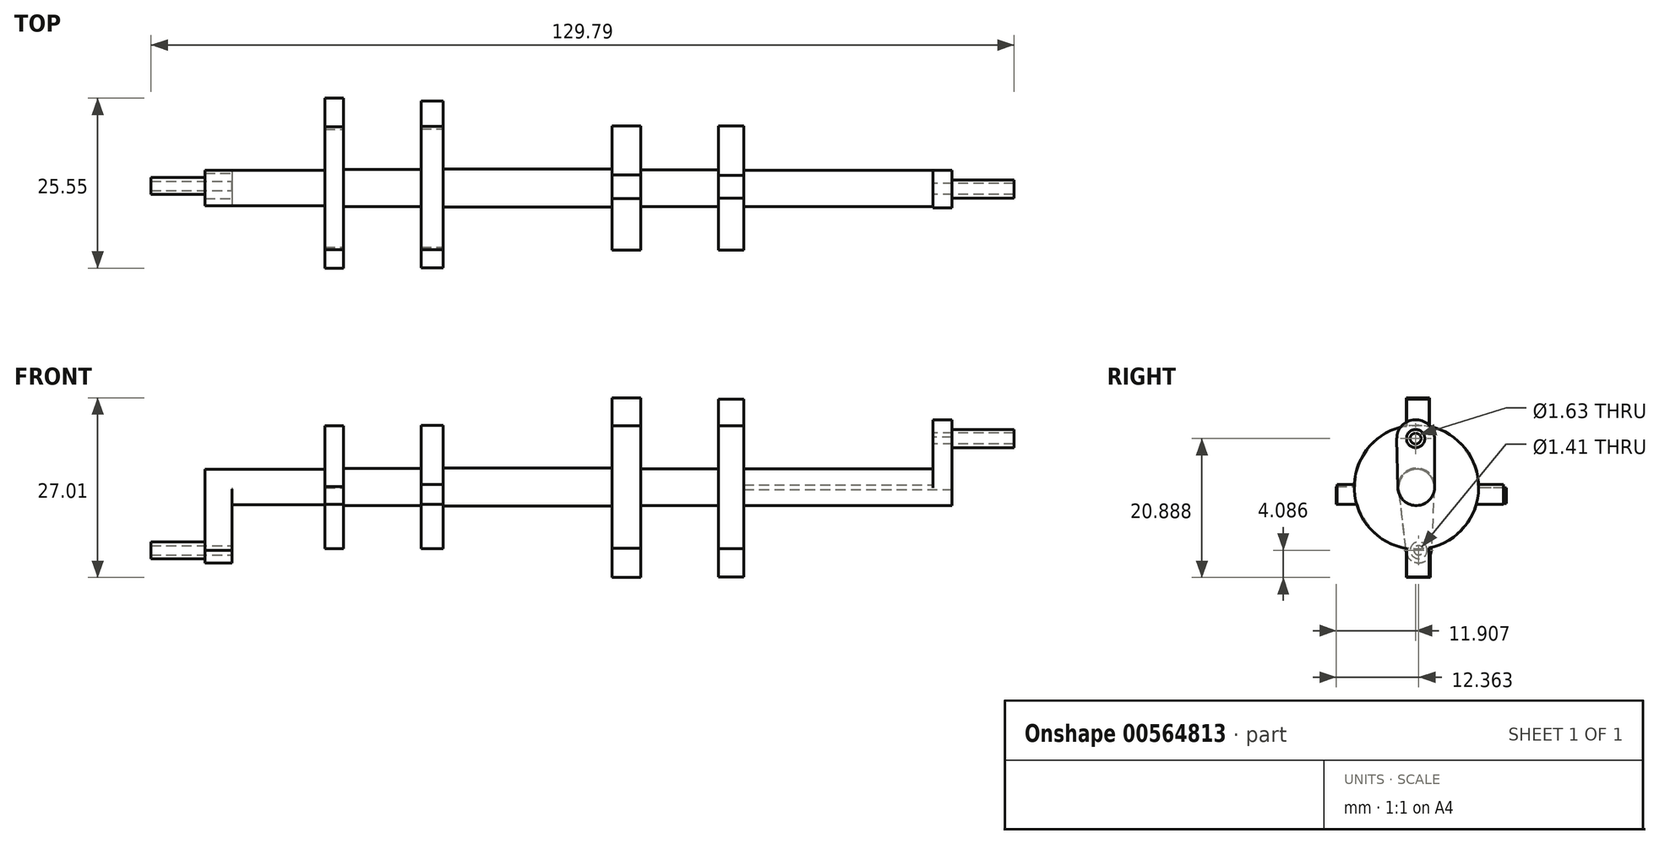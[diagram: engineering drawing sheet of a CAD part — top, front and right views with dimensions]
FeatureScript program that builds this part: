
annotation { "Feature Type Name" : "Feature", "Feature Type Description" : "" }
export const myFeature = defineFeature(function(context is Context, id is Id, definition is map)
    precondition{}
    {
        {
            var Q0;
            Q0=qCreatedBy(makeId("Right.planeOp"),FACE);
            var sketch = newSketch(context, id + "F0", { "sketchPlane" : qUnion([Q0])});
            skCircle(sketch, "E0", {"center": v(23.37, 56.05) * mm, "radius": 1.37 * mm});
            skCircle(sketch, "E1", {"center": v(23.46, 48.73) * mm, "radius": 2.75 * mm});
            skLineSegment(sketch, "E2", {"start": v(26.2, 48.37) * mm, "end": v(26.2, 56.23) * mm});
            skLineSegment(sketch, "E3", {"start": v(20.71, 48.66) * mm, "end": v(20.54, 55.98) * mm});
            skArc(sketch, "E4", {"start": v(26.2, 56.23) * mm, "mid": v(23.24, 58.88) * mm, "end": v(20.54, 55.98) * mm});
            skCircle(sketch, "E5", {"center": v(23.37, 56.05) * mm, "radius": 0.81 * mm});
            skSolve(sketch);
        }
        {
            var Q0;
            Q0=makeQuery(id+"F0.imprint","IMPRINT",FACE,{"disambiguationData":[TD([[makeQuery(id+"F0.imprint","IMPRINT",EDGE,{"derivedFrom":sQuery(id+"F0.wireOp",EDGE,"E0")}),1.0]])]});
            extrude(context, id + "F1", {"entities" : qUnion([Q0]), "depth" : 12.2 * mm, "offsetDistance" : 25.4 * mm});
        }
        {
            var Q0;
            Q0=makeQuery(id+"F0.imprint","IMPRINT",FACE,{"disambiguationData":[TD([[makeQuery(id+"F0.imprint","IMPRINT",EDGE,{"derivedFrom":sQuery(id+"F0.wireOp",EDGE,"E1")}),1.0]])]});
            extrude(context, id + "F2", {"entities" : qUnion([Q0]), "operationType" : NewBodyOperationType.ADD, "oppositeDirection" : true, "depth" : 28.45 * mm, "offsetDistance" : 25.4 * mm});
        }
        {
            var Q0;
            Q0=makeQuery(id+"F2.opExtrude","CAP_FACE",FACE,{"disambiguationData":[OSD([sQuery(id+"F0.wireOp",EDGE,"E1")])],"isStart":false});
            var sketch = newSketch(context, id + "F3", { "sketchPlane" : qUnion([Q0])});
            skSolve(sketch);
        }
        {
            var Q0;
            Q0=makeQuery(id+"F3.imprint","IMPRINT",FACE,{"disambiguationData":[TD([[makeQuery(id+"F3.imprint","IMPRINT",EDGE,{"derivedFrom":makeQuery(id+"F2.opExtrude","CAP_EDGE",EDGE,{"disambiguationData":[OSD([sQuery(id+"F0.wireOp",EDGE,"E1")])],"isStart":false})}),-1.0]])]});
            var sketch = newSketch(context, id + "F4", { "sketchPlane" : qUnion([Q0])});
            skCircle(sketch, "E6", {"center": v(-23.5, 48.74) * mm, "radius": 9.35 * mm});
            skLineSegment(sketch, "E7", {"start": v(-25.42, 57.9) * mm, "end": v(-25.42, 61.98) * mm});
            skLineSegment(sketch, "E8", {"start": v(-25.42, 61.98) * mm, "end": v(-22, 61.98) * mm});
            skLineSegment(sketch, "E9", {"start": v(-22, 61.98) * mm, "end": v(-22, 57.98) * mm});
            skLineSegment(sketch, "E10", {"start": v(-25.42, 39.59) * mm, "end": v(-25.42, 35.2) * mm});
            skLineSegment(sketch, "E11", {"start": v(-25.42, 35.2) * mm, "end": v(-22, 35.2) * mm});
            skLineSegment(sketch, "E12", {"start": v(-22, 35.2) * mm, "end": v(-22, 39.51) * mm});
            skSolve(sketch);
        }
        {
            var Q0;
            Q0=makeQuery(id+"F3.imprint","IMPRINT",FACE,{"disambiguationData":[TD([[makeQuery(id+"F3.imprint","IMPRINT",EDGE,{"derivedFrom":makeQuery(id+"F2.opExtrude","CAP_EDGE",EDGE,{"disambiguationData":[OSD([sQuery(id+"F0.wireOp",EDGE,"E1")])],"isStart":false})}),-1.0]])]});
            var Q1;
            {var subQ0=sQuery(id+"F4.wireOp",EDGE,"E10");Q1=makeQuery(id+"F4.imprint","IMPRINT",FACE,{"disambiguationData":[TD([[makeQuery(id+"F4.imprint","IMPRINT",EDGE,{"derivedFrom":subQ0}),1.0]])]});}
            var Q2;
            {var subQ0=sQuery(id+"F4.wireOp",EDGE,"E7");Q2=makeQuery(id+"F4.imprint","IMPRINT",FACE,{"disambiguationData":[TD([[makeQuery(id+"F4.imprint","IMPRINT",EDGE,{"derivedFrom":subQ0}),-1.0]])]});}
            var Q3;
            Q3=makeQuery(id+"F4.imprint","IMPRINT",FACE,{"disambiguationData":[TD([[makeQuery(id+"F4.imprint","IMPRINT",EDGE,{"derivedFrom":makeQuery(id+"F3.imprint","IMPRINT",EDGE,{"derivedFrom":makeQuery(id+"F2.opExtrude","CAP_EDGE",EDGE,{"disambiguationData":[OSD([sQuery(id+"F0.wireOp",EDGE,"E1")])],"isStart":false})})}),1.0]])]});
            extrude(context, id + "F5", {"entities" : qUnion([Q0, Q1, Q2, Q3]), "operationType" : NewBodyOperationType.ADD, "depth" : 3.8 * mm, "offsetDistance" : 25.4 * mm});
        }
        {
            var Q0;
            {var subQ0=sQuery(id+"F0.wireOp",EDGE,"E1");Q0=makeQuery(id+"F5.boolean.opBoolean","MERGE",FACE,{"derivedFrom":[makeQuery(id+"F5.opExtrude","CAP_FACE",FACE,{"disambiguationData":[OSD([subQ0])],"isStart":false}),makeQuery(id+"F5.opExtrude","CAP_FACE",FACE,{"disambiguationData":[OSD([subQ0,sQuery(id+"F4.wireOp",EDGE,"E6"),sQuery(id+"F4.wireOp",EDGE,"E7"),sQuery(id+"F4.wireOp",EDGE,"E8"),sQuery(id+"F4.wireOp",EDGE,"E9"),sQuery(id+"F4.wireOp",EDGE,"E10"),sQuery(id+"F4.wireOp",EDGE,"E11"),sQuery(id+"F4.wireOp",EDGE,"E12")])],"isStart":false})]});}
            var sketch = newSketch(context, id + "F6", { "sketchPlane" : qUnion([Q0])});
            skCircle(sketch, "E13", {"center": v(-23.5, 48.74) * mm, "radius": 2.76 * mm});
            skSolve(sketch);
        }
        {
            var Q0;
            Q0=makeQuery(id+"F6.imprint","IMPRINT",FACE,{"disambiguationData":[TD([[makeQuery(id+"F6.imprint","IMPRINT",EDGE,{"derivedFrom":sQuery(id+"F6.wireOp",EDGE,"E13")}),1.0]])]});
            extrude(context, id + "F7", {"entities" : qUnion([Q0]), "operationType" : NewBodyOperationType.ADD, "depth" : 11.68 * mm, "offsetDistance" : 25.4 * mm});
        }
        {
            var Q0;
            Q0=makeQuery(id+"F7.opExtrude","CAP_FACE",FACE,{"disambiguationData":[OSD([sQuery(id+"F6.wireOp",EDGE,"E13")])],"isStart":false});
            var sketch = newSketch(context, id + "F8", { "sketchPlane" : qUnion([Q0])});
            skCircle(sketch, "E14", {"center": v(-23.5, 48.74) * mm, "radius": 9.35 * mm});
            skLineSegment(sketch, "E15", {"start": v(-25.45, 57.89) * mm, "end": v(-25.45, 62.17) * mm});
            skLineSegment(sketch, "E16", {"start": v(-25.45, 62.17) * mm, "end": v(-21.95, 62.17) * mm});
            skLineSegment(sketch, "E17", {"start": v(-21.95, 62.17) * mm, "end": v(-21.95, 57.97) * mm});
            skLineSegment(sketch, "E18", {"start": v(-21.95, 39.52) * mm, "end": v(-21.95, 35.16) * mm});
            skLineSegment(sketch, "E19", {"start": v(-21.95, 35.16) * mm, "end": v(-25.56, 35.16) * mm});
            skLineSegment(sketch, "E20", {"start": v(-25.56, 35.16) * mm, "end": v(-25.56, 39.62) * mm});
            skSolve(sketch);
        }
        {
            var Q0;
            Q0=makeQuery(id+"F8.imprint","IMPRINT",FACE,{"disambiguationData":[TD([[makeQuery(id+"F8.imprint","IMPRINT",EDGE,{"derivedFrom":makeQuery(id+"F7.opExtrude","CAP_EDGE",EDGE,{"disambiguationData":[OSD([sQuery(id+"F6.wireOp",EDGE,"E13")])],"isStart":false})}),1.0]])]});
            var Q1;
            Q1=makeQuery(id+"F8.imprint","IMPRINT",FACE,{"disambiguationData":[TD([[makeQuery(id+"F8.imprint","IMPRINT",EDGE,{"derivedFrom":makeQuery(id+"F7.opExtrude","CAP_EDGE",EDGE,{"disambiguationData":[OSD([sQuery(id+"F6.wireOp",EDGE,"E13")])],"isStart":false})}),-1.0]])]});
            var Q2;
            {var subQ0=sQuery(id+"F8.wireOp",EDGE,"E15");Q2=makeQuery(id+"F8.imprint","IMPRINT",FACE,{"disambiguationData":[TD([[makeQuery(id+"F8.imprint","IMPRINT",EDGE,{"derivedFrom":subQ0}),-1.0]])]});}
            var Q3;
            {var subQ0=sQuery(id+"F8.wireOp",EDGE,"E18");Q3=makeQuery(id+"F8.imprint","IMPRINT",FACE,{"disambiguationData":[TD([[makeQuery(id+"F8.imprint","IMPRINT",EDGE,{"derivedFrom":subQ0}),-1.0]])]});}
            extrude(context, id + "F9", {"entities" : qUnion([Q0, Q1, Q2, Q3]), "operationType" : NewBodyOperationType.ADD, "depth" : 4.32 * mm, "offsetDistance" : 25.4 * mm});
        }
        {
            var Q0;
            Q0=makeQuery(id+"F9.opExtrude","CAP_FACE",FACE,{"disambiguationData":[OSD([sQuery(id+"F8.wireOp",EDGE,"E14"),sQuery(id+"F8.wireOp",EDGE,"E15"),sQuery(id+"F8.wireOp",EDGE,"E16"),sQuery(id+"F8.wireOp",EDGE,"E17"),sQuery(id+"F8.wireOp",EDGE,"E18"),sQuery(id+"F8.wireOp",EDGE,"E19"),sQuery(id+"F8.wireOp",EDGE,"E20")])],"isStart":false});
            var sketch = newSketch(context, id + "F10", { "sketchPlane" : qUnion([Q0])});
            skCircle(sketch, "E21", {"center": v(-23.5, 48.74) * mm, "radius": 2.85 * mm});
            skSolve(sketch);
        }
        {
            var Q0;
            Q0=makeQuery(id+"F10.imprint","IMPRINT",FACE,{"disambiguationData":[TD([[makeQuery(id+"F10.imprint","IMPRINT",EDGE,{"derivedFrom":sQuery(id+"F10.wireOp",EDGE,"E21")}),1.0]])]});
            extrude(context, id + "F11", {"entities" : qUnion([Q0]), "operationType" : NewBodyOperationType.ADD, "depth" : 25.4 * mm, "offsetDistance" : 25.4 * mm});
        }
        {
            var Q0;
            Q0=makeQuery(id+"F11.opExtrude","CAP_FACE",FACE,{"disambiguationData":[OSD([sQuery(id+"F10.wireOp",EDGE,"E21")])],"isStart":false});
            var sketch = newSketch(context, id + "F12", { "sketchPlane" : qUnion([Q0])});
            skCircle(sketch, "E22", {"center": v(-23.5, 48.74) * mm, "radius": 9.28 * mm});
            skLineSegment(sketch, "E23", {"start": v(-32.42, 46.15) * mm, "end": v(-36.57, 46.15) * mm});
            skLineSegment(sketch, "E24", {"start": v(-36.57, 46.15) * mm, "end": v(-36.57, 49.16) * mm});
            skLineSegment(sketch, "E25", {"start": v(-36.57, 49.16) * mm, "end": v(-32.78, 49.16) * mm});
            skLineSegment(sketch, "E26", {"start": v(-14.23, 49.16) * mm, "end": v(-11.53, 49.16) * mm});
            skLineSegment(sketch, "E27", {"start": v(-11.53, 49.16) * mm, "end": v(-11.53, 46.15) * mm});
            skLineSegment(sketch, "E28", {"start": v(-11.53, 46.15) * mm, "end": v(-14.59, 46.15) * mm});
            skSolve(sketch);
        }
        {
            var Q0;
            Q0=makeQuery(id+"F12.imprint","IMPRINT",FACE,{"disambiguationData":[TD([[makeQuery(id+"F12.imprint","IMPRINT",EDGE,{"derivedFrom":makeQuery(id+"F11.opExtrude","CAP_EDGE",EDGE,{"disambiguationData":[OSD([sQuery(id+"F10.wireOp",EDGE,"E21")])],"isStart":false})}),1.0]])]});
            var Q1;
            Q1=makeQuery(id+"F12.imprint","IMPRINT",FACE,{"disambiguationData":[TD([[makeQuery(id+"F12.imprint","IMPRINT",EDGE,{"derivedFrom":makeQuery(id+"F11.opExtrude","CAP_EDGE",EDGE,{"disambiguationData":[OSD([sQuery(id+"F10.wireOp",EDGE,"E21")])],"isStart":false})}),-1.0]])]});
            var Q2;
            {var subQ0=sQuery(id+"F12.wireOp",EDGE,"E26");Q2=makeQuery(id+"F12.imprint","IMPRINT",FACE,{"disambiguationData":[TD([[makeQuery(id+"F12.imprint","IMPRINT",EDGE,{"derivedFrom":subQ0}),-1.0]])]});}
            var Q3;
            {var subQ0=sQuery(id+"F12.wireOp",EDGE,"E23");Q3=makeQuery(id+"F12.imprint","IMPRINT",FACE,{"disambiguationData":[TD([[makeQuery(id+"F12.imprint","IMPRINT",EDGE,{"derivedFrom":subQ0}),-1.0]])]});}
            extrude(context, id + "F13", {"entities" : qUnion([Q0, Q1, Q2, Q3]), "operationType" : NewBodyOperationType.ADD, "depth" : 3.3 * mm, "offsetDistance" : 25.4 * mm});
        }
        {
            var Q0;
            Q0=makeQuery(id+"F13.opExtrude","CAP_FACE",FACE,{"disambiguationData":[OSD([sQuery(id+"F12.wireOp",EDGE,"E22"),sQuery(id+"F12.wireOp",EDGE,"E23"),sQuery(id+"F12.wireOp",EDGE,"E24"),sQuery(id+"F12.wireOp",EDGE,"E25"),sQuery(id+"F12.wireOp",EDGE,"E26"),sQuery(id+"F12.wireOp",EDGE,"E27"),sQuery(id+"F12.wireOp",EDGE,"E28")])],"isStart":false});
            var sketch = newSketch(context, id + "F14", { "sketchPlane" : qUnion([Q0])});
            skCircle(sketch, "E29", {"center": v(-23.5, 48.74) * mm, "radius": 2.8 * mm});
            skSolve(sketch);
        }
        {
            var Q0;
            Q0=makeQuery(id+"F14.imprint","IMPRINT",FACE,{"disambiguationData":[TD([[makeQuery(id+"F14.imprint","IMPRINT",EDGE,{"derivedFrom":sQuery(id+"F14.wireOp",EDGE,"E29")}),1.0]])]});
            extrude(context, id + "F15", {"entities" : qUnion([Q0]), "operationType" : NewBodyOperationType.ADD, "depth" : 11.68 * mm, "offsetDistance" : 25.4 * mm});
        }
        {
            var Q0;
            Q0=makeQuery(id+"F15.opExtrude","CAP_FACE",FACE,{"disambiguationData":[OSD([sQuery(id+"F14.wireOp",EDGE,"E29")])],"isStart":false});
            var sketch = newSketch(context, id + "F16", { "sketchPlane" : qUnion([Q0])});
            skCircle(sketch, "E30", {"center": v(-23.5, 48.74) * mm, "radius": 9.24 * mm});
            skLineSegment(sketch, "E31", {"start": v(-32.37, 46.15) * mm, "end": v(-37.01, 46.26) * mm});
            skLineSegment(sketch, "E32", {"start": v(-37.01, 46.26) * mm, "end": v(-37.01, 48.66) * mm});
            skLineSegment(sketch, "E33", {"start": v(-37.01, 48.66) * mm, "end": v(-32.74, 48.66) * mm});
            skLineSegment(sketch, "E34", {"start": v(-14.64, 46.15) * mm, "end": v(-11.46, 46.15) * mm});
            skLineSegment(sketch, "E35", {"start": v(-11.46, 46.15) * mm, "end": v(-11.46, 48.8) * mm});
            skLineSegment(sketch, "E36", {"start": v(-11.46, 48.8) * mm, "end": v(-14.27, 48.8) * mm});
            skSolve(sketch);
        }
        {
            var Q0;
            Q0=makeQuery(id+"F16.imprint","IMPRINT",FACE,{"disambiguationData":[TD([[makeQuery(id+"F16.imprint","IMPRINT",EDGE,{"derivedFrom":makeQuery(id+"F15.opExtrude","CAP_EDGE",EDGE,{"disambiguationData":[OSD([sQuery(id+"F14.wireOp",EDGE,"E29")])],"isStart":false})}),1.0]])]});
            var Q1;
            Q1=makeQuery(id+"F16.imprint","IMPRINT",FACE,{"disambiguationData":[TD([[makeQuery(id+"F16.imprint","IMPRINT",EDGE,{"derivedFrom":makeQuery(id+"F15.opExtrude","CAP_EDGE",EDGE,{"disambiguationData":[OSD([sQuery(id+"F14.wireOp",EDGE,"E29")])],"isStart":false})}),-1.0]])]});
            var Q2;
            {var subQ0=sQuery(id+"F16.wireOp",EDGE,"E31");Q2=makeQuery(id+"F16.imprint","IMPRINT",FACE,{"disambiguationData":[TD([[makeQuery(id+"F16.imprint","IMPRINT",EDGE,{"derivedFrom":subQ0}),-1.0]])]});}
            var Q3;
            {var subQ0=sQuery(id+"F16.wireOp",EDGE,"E34");Q3=makeQuery(id+"F16.imprint","IMPRINT",FACE,{"disambiguationData":[TD([[makeQuery(id+"F16.imprint","IMPRINT",EDGE,{"derivedFrom":subQ0}),1.0]])]});}
            extrude(context, id + "F17", {"entities" : qUnion([Q0, Q1, Q2, Q3]), "operationType" : NewBodyOperationType.ADD, "depth" : 2.8 * mm, "offsetDistance" : 25.4 * mm});
        }
        {
            var Q0;
            Q0=makeQuery(id+"F17.opExtrude","CAP_FACE",FACE,{"disambiguationData":[OSD([sQuery(id+"F16.wireOp",EDGE,"E30"),sQuery(id+"F16.wireOp",EDGE,"E31"),sQuery(id+"F16.wireOp",EDGE,"E32"),sQuery(id+"F16.wireOp",EDGE,"E33"),sQuery(id+"F16.wireOp",EDGE,"E34"),sQuery(id+"F16.wireOp",EDGE,"E35"),sQuery(id+"F16.wireOp",EDGE,"E36")])],"isStart":false});
            var sketch = newSketch(context, id + "F18", { "sketchPlane" : qUnion([Q0])});
            skCircle(sketch, "E37", {"center": v(-23.5, 48.74) * mm, "radius": 2.68 * mm});
            skSolve(sketch);
        }
        {
            var Q0;
            Q0=makeQuery(id+"F18.imprint","IMPRINT",FACE,{"disambiguationData":[TD([[makeQuery(id+"F18.imprint","IMPRINT",EDGE,{"derivedFrom":sQuery(id+"F18.wireOp",EDGE,"E37")}),1.0]])]});
            extrude(context, id + "F19", {"entities" : qUnion([Q0]), "operationType" : NewBodyOperationType.ADD, "depth" : 13.97 * mm, "offsetDistance" : 25.4 * mm});
        }
        {
            var Q0;
            Q0=makeQuery(id+"F19.opExtrude","CAP_FACE",FACE,{"disambiguationData":[OSD([sQuery(id+"F18.wireOp",EDGE,"E37")])],"isStart":false});
            var sketch = newSketch(context, id + "F20", { "sketchPlane" : qUnion([Q0])});
            skLineSegment(sketch, "E38", {"start": v(-26.18, 48.61) * mm, "end": v(-25.72, 39.25) * mm});
            skArc(sketch, "E39", {"start": v(-25.72, 39.25) * mm, "mid": v(-23.82, 37.35) * mm, "end": v(-21.93, 39.25) * mm});
            skLineSegment(sketch, "E40", {"start": v(-21.93, 39.25) * mm, "end": v(-20.84, 48.43) * mm});
            skArc(sketch, "E41", {"start": v(-20.84, 48.43) * mm, "mid": v(-23.41, 51.42) * mm, "end": v(-26.18, 48.61) * mm});
            skCircle(sketch, "E42", {"center": v(-23.82, 39.25) * mm, "radius": 1.26 * mm});
            skCircle(sketch, "E43", {"center": v(-23.82, 39.25) * mm, "radius": 0.7 * mm});
            skSolve(sketch);
        }
        {
            var Q0;
            {var subQ0=sQuery(id+"F20.wireOp",EDGE,"E41");Q0=makeQuery(id+"F20.imprint","IMPRINT",FACE,{"disambiguationData":[TD([[makeQuery(id+"F20.imprint","IMPRINT",EDGE,{"derivedFrom":subQ0}),1.0]])]});}
            var Q1;
            {var subQ1=sQuery(id+"F20.wireOp",EDGE,"E38");Q1=makeQuery(id+"F20.imprint","IMPRINT",FACE,{"disambiguationData":[TD([[makeQuery(id+"F20.imprint","IMPRINT",EDGE,{"derivedFrom":subQ1}),1.0]])]});}
            extrude(context, id + "F21", {"entities" : qUnion([Q0, Q1]), "operationType" : NewBodyOperationType.ADD, "depth" : 4.06 * mm, "offsetDistance" : 25.4 * mm});
        }
        {
            var Q0;
            Q0=makeQuery(id+"F20.imprint","IMPRINT",FACE,{"disambiguationData":[TD([[makeQuery(id+"F20.imprint","IMPRINT",EDGE,{"derivedFrom":sQuery(id+"F20.wireOp",EDGE,"E42")}),1.0]])]});
            extrude(context, id + "F22", {"entities" : qUnion([Q0]), "operationType" : NewBodyOperationType.ADD, "depth" : 12.2 * mm, "offsetDistance" : 25.4 * mm});
        }
        {
            var Q0;
            {var subQ0=sQuery(id+"F0.wireOp",EDGE,"E1");var subQ1=makeQuery(id+"F0.imprint","INTERSECT",VERTEX,{"derivedFrom":[subQ0,sQuery(id+"F0.wireOp",EDGE,"E3")]});Q0=makeQuery(id+"F0.imprint","IMPRINT",FACE,{"disambiguationData":[TD([[makeQuery(id+"F0.imprint","IMPRINT",EDGE,{"disambiguationData":[TD([[subQ1,1.0]])],"derivedFrom":subQ0}),1.0]])]});}
            var Q1;
            Q1=makeQuery(id+"F0.imprint","IMPRINT",FACE,{"disambiguationData":[TD([[makeQuery(id+"F0.imprint","IMPRINT",EDGE,{"derivedFrom":sQuery(id+"F0.wireOp",EDGE,"E0")}),-1.0]])]});
            extrude(context, id + "F23", {"entities" : qUnion([Q0, Q1]), "operationType" : NewBodyOperationType.ADD, "depth" : 2.87 * mm, "offsetDistance" : 25.4 * mm});
        }
    });
